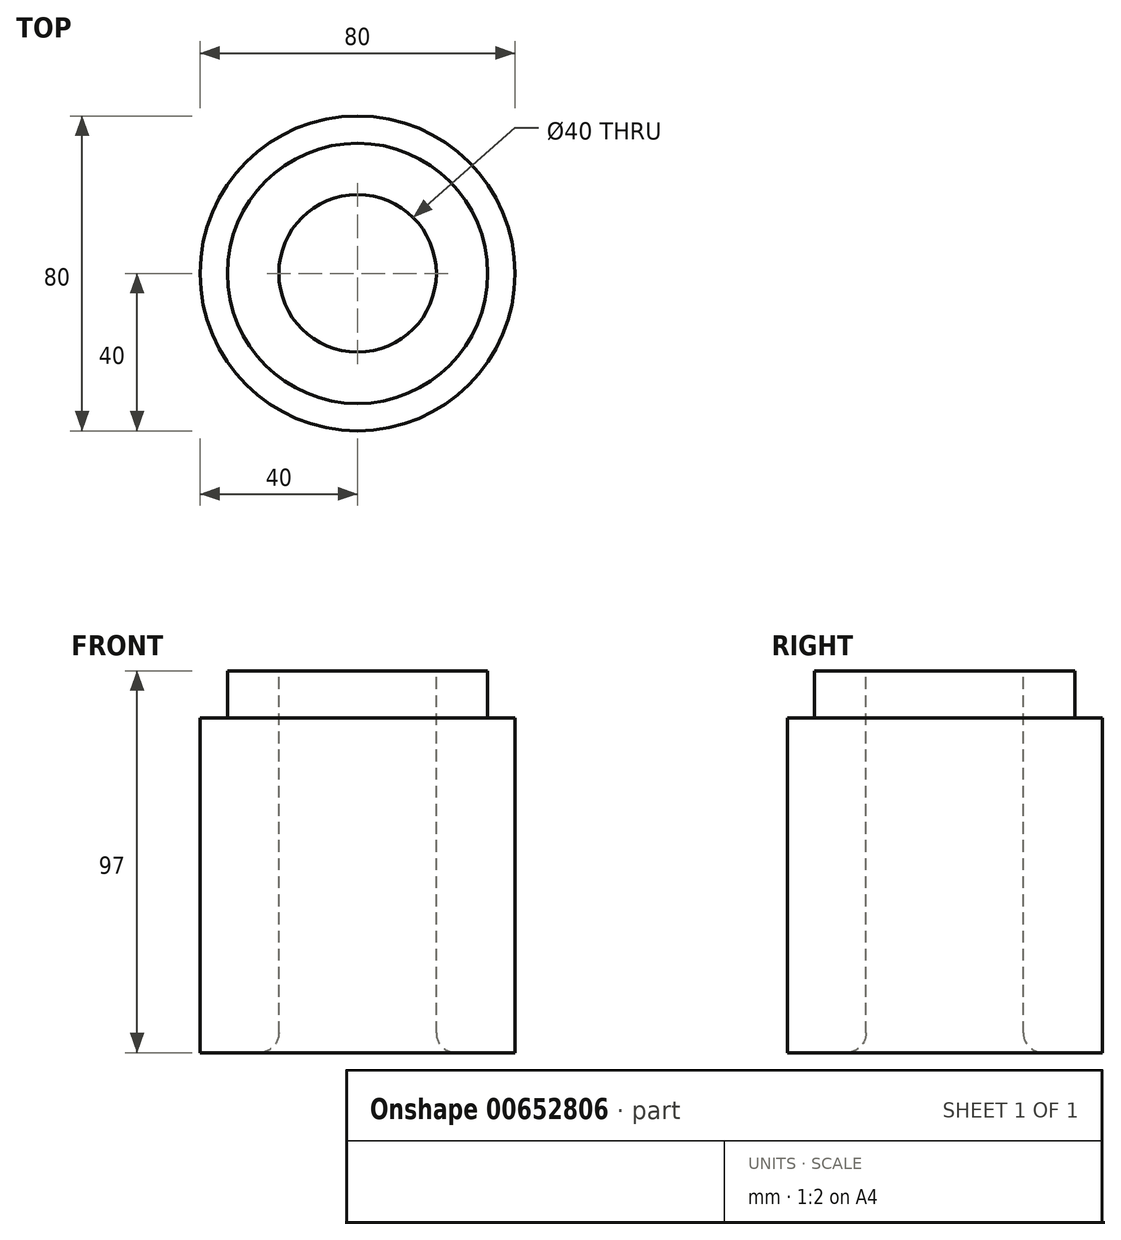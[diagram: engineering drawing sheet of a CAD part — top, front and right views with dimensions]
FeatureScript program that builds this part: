
annotation { "Feature Type Name" : "Feature", "Feature Type Description" : "" }
export const myFeature = defineFeature(function(context is Context, id is Id, definition is map)
    precondition{}
    {
        {
            var Q0;
            Q0=qCreatedBy(makeId("Top.planeOp"),FACE);
            var sketch = newSketch(context, id + "F0", { "sketchPlane" : qUnion([Q0])});
            skCircle(sketch, "E0", {"center": v(0, 0) * mm, "radius": 40 * mm});
            skSolve(sketch);
        }
        {
            var Q0;
            Q0 = qSketchRegion(id + "F0", true);
            extrude(context, id + "F1", {"entities" : qUnion([Q0]), "depth" : 85 * mm, "offsetDistance" : 25 * mm});
        }
        {
            var Q0;
            Q0=makeQuery(id+"F1.opExtrude","CAP_FACE",FACE,{"disambiguationData":[OSD([sQuery(id+"F0.wireOp",EDGE,"E0")])],"isStart":false});
            var sketch = newSketch(context, id + "F2", { "sketchPlane" : qUnion([Q0])});
            skCircle(sketch, "E1", {"center": v(0, 0) * mm, "radius": 20 * mm});
            skSolve(sketch);
        }
        {
            var Q0;
            Q0=makeQuery(id+"F2.imprint","IMPRINT",FACE,{"disambiguationData":[TD([[makeQuery(id+"F2.imprint","IMPRINT",EDGE,{"derivedFrom":sQuery(id+"F2.wireOp",EDGE,"E1")}),1.0]])]});
            extrude(context, id + "F3", {"entities" : qUnion([Q0]), "operationType" : NewBodyOperationType.REMOVE, "oppositeDirection" : true, "depth" : 88 * mm, "offsetDistance" : 25 * mm});
        }
        {
            var Q0;
            Q0=makeQuery(id+"F3.boolean.opBoolean","INTERSECT",EDGE,{"derivedFrom":[makeQuery(id+"F1.opExtrude","CAP_FACE",FACE,{"disambiguationData":[OSD([sQuery(id+"F0.wireOp",EDGE,"E0")])],"isStart":true}),makeQuery(id+"F3.opExtrude","SWEPT_FACE",FACE,{"disambiguationData":[OSD([sQuery(id+"F2.wireOp",EDGE,"E1")])]})]});
            fillet(context, id + "F4", {"entities" : qUnion([Q0]), "radius" : 5 * mm, "tangentPropagation" : true, "allowEdgeOverflow" : false});
        }
        {
            var Q0;
            Q0=makeQuery(id+"F1.opExtrude","CAP_FACE",FACE,{"disambiguationData":[OSD([sQuery(id+"F0.wireOp",EDGE,"E0")])],"isStart":false});
            var sketch = newSketch(context, id + "F5", { "sketchPlane" : qUnion([Q0])});
            skCircle(sketch, "E2", {"center": v(0, 0) * mm, "radius": 33.06 * mm});
            skSolve(sketch);
        }
        {
            var Q0;
            Q0=makeQuery(id+"F5.imprint","IMPRINT",FACE,{"disambiguationData":[TD([[makeQuery(id+"F5.imprint","IMPRINT",EDGE,{"derivedFrom":sQuery(id+"F5.wireOp",EDGE,"E2")}),1.0]])]});
            extrude(context, id + "F6", {"entities" : qUnion([Q0]), "operationType" : NewBodyOperationType.ADD, "depth" : 12 * mm, "offsetDistance" : 25 * mm});
        }
    });
